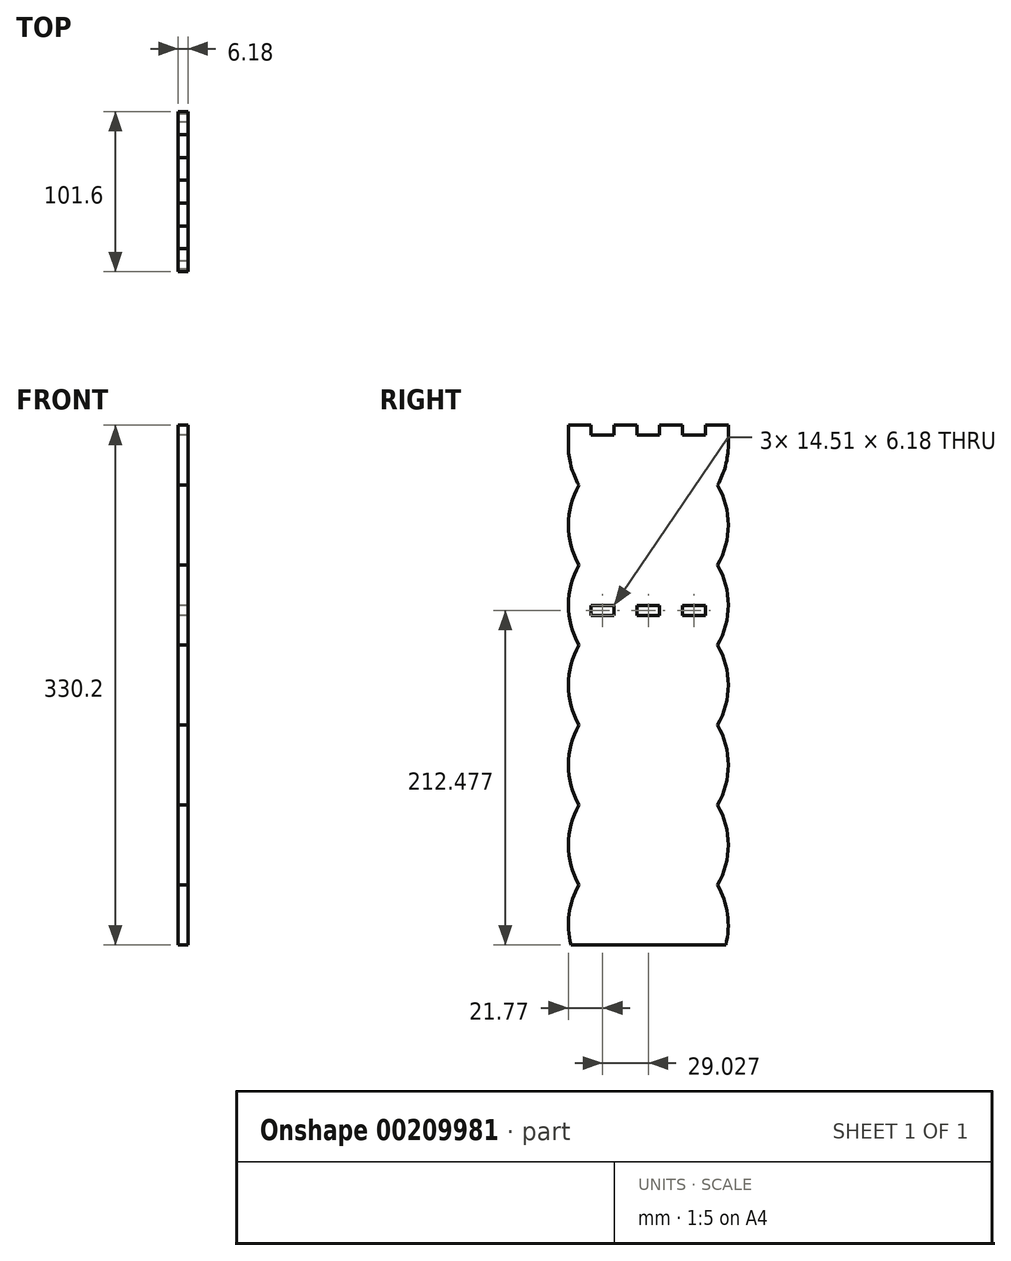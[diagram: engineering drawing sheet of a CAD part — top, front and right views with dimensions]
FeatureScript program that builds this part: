
annotation { "Feature Type Name" : "Feature", "Feature Type Description" : "" }
export const myFeature = defineFeature(function(context is Context, id is Id, definition is map)
    precondition{}
    {
        {
            var Q0;
            Q0=qCreatedBy(makeId("Right.planeOp"),FACE);
            var sketch = newSketch(context, id + "F0", { "sketchPlane" : qUnion([Q0])});
            skLineSegment(sketch, "E0.bottom", {"start": v(49.19, -165.1) * mm, "end": v(-49.19, -165.1) * mm});
            skLineSegment(sketch, "E0.top", {"start": v(50.8, 165.1) * mm, "end": v(36.28, 165.1) * mm});
            skPoint(sketch, "E0.middle", {"position": v(0, 0) * mm});
            skArc(sketch, "E1", {"start": v(-44, 25.4) * mm, "mid": v(-50.8, 0) * mm, "end": v(-44, -25.4) * mm});
            skArc(sketch, "E2", {"start": v(-44, 76.2) * mm, "mid": v(-50.8, 50.8) * mm, "end": v(-44, 25.4) * mm});
            skArc(sketch, "E3", {"start": v(-44, 127) * mm, "mid": v(-50.8, 101.6) * mm, "end": v(-44, 76.2) * mm});
            skArc(sketch, "E4", {"start": v(-50.8, 152.4) * mm, "mid": v(-49.07, 139.25) * mm, "end": v(-44, 127) * mm});
            skArc(sketch, "E5", {"start": v(-44, -25.4) * mm, "mid": v(-50.8, -50.8) * mm, "end": v(-44, -76.2) * mm});
            skArc(sketch, "E6", {"start": v(-44, -76.2) * mm, "mid": v(-50.8, -101.6) * mm, "end": v(-44, -127) * mm});
            skArc(sketch, "E7", {"start": v(-44, -127) * mm, "mid": v(-50.33, -145.54) * mm, "end": v(-49.19, -165.1) * mm});
            skPoint(sketch, "E8.orphan", {"position": v(0, 165.1) * mm});
            skLineSegment(sketch, "E9.trimOffspring", {"start": v(-50.8, 152.4) * mm, "end": v(-50.8, 165.1) * mm});
            skLineSegment(sketch, "E10.trimOffspring", {"start": v(50.8, 152.4) * mm, "end": v(50.8, 165.1) * mm});
            skArc(sketch, "E11.trimOffspring", {"start": v(44, 76.2) * mm, "mid": v(50.8, 101.6) * mm, "end": v(44, 127) * mm});
            skArc(sketch, "E12.trimOffspring", {"start": v(44, 127) * mm, "mid": v(49.07, 139.25) * mm, "end": v(50.8, 152.4) * mm});
            skArc(sketch, "E13.trimOffspring", {"start": v(44, 25.4) * mm, "mid": v(50.8, 50.8) * mm, "end": v(44, 76.2) * mm});
            skArc(sketch, "E14.trimOffspring", {"start": v(44, -25.4) * mm, "mid": v(50.8, 0) * mm, "end": v(44, 25.4) * mm});
            skArc(sketch, "E15.trimOffspring", {"start": v(44, -76.2) * mm, "mid": v(50.8, -50.8) * mm, "end": v(44, -25.4) * mm});
            skArc(sketch, "E16.trimOffspring", {"start": v(44, -127) * mm, "mid": v(50.8, -101.6) * mm, "end": v(44, -76.2) * mm});
            skArc(sketch, "E17.trimOffspring", {"start": v(49.19, -165.1) * mm, "mid": v(50.33, -145.54) * mm, "end": v(44, -127) * mm});
            skPoint(sketch, "E18.trimOffspring.end.orphan", {"position": v(0, -165.1) * mm});
            skPoint(sketch, "E19.orphan", {"position": v(-50.8, -165.1) * mm});
            skPoint(sketch, "E20.orphan", {"position": v(50.8, -165.1) * mm});
            skLineSegment(sketch, "E21", {"start": v(-36.29, 165.1) * mm, "end": v(-36.29, 158.92) * mm});
            skLineSegment(sketch, "E22", {"start": v(-36.29, 158.92) * mm, "end": v(-21.77, 158.92) * mm});
            skLineSegment(sketch, "E23", {"start": v(-21.77, 158.92) * mm, "end": v(-21.77, 165.1) * mm});
            skLineSegment(sketch, "E24", {"start": v(-7.26, 165.1) * mm, "end": v(-7.26, 158.92) * mm});
            skLineSegment(sketch, "E25", {"start": v(-7.26, 158.92) * mm, "end": v(0, 158.92) * mm});
            skLineSegment(sketch, "E26.trimOffspring", {"start": v(-36.29, 165.1) * mm, "end": v(-50.8, 165.1) * mm});
            skLineSegment(sketch, "E27.MirrorCS", {"start": v(7.25, 158.92) * mm, "end": v(0, 158.92) * mm});
            skLineSegment(sketch, "E28.MirrorCS", {"start": v(7.25, 165.1) * mm, "end": v(7.25, 158.92) * mm});
            skLineSegment(sketch, "E29.MirrorCS", {"start": v(36.28, 158.92) * mm, "end": v(21.77, 158.92) * mm});
            skLineSegment(sketch, "E30.MirrorCS", {"start": v(-50.8, 165.1) * mm, "end": v(-36.29, 165.1) * mm});
            skLineSegment(sketch, "E31.MirrorCS", {"start": v(36.28, 165.1) * mm, "end": v(36.28, 158.92) * mm});
            skLineSegment(sketch, "E32.MirrorCS", {"start": v(21.77, 158.92) * mm, "end": v(21.77, 165.1) * mm});
            skLineSegment(sketch, "E33.trimOffspring", {"start": v(0, 165.1) * mm, "end": v(0, 165.1) * mm});
            skLineSegment(sketch, "E34.trimOffspring", {"start": v(7.25, 165.1) * mm, "end": v(21.77, 165.1) * mm});
            skLineSegment(sketch, "E35.trimOffspring", {"start": v(-21.77, 165.1) * mm, "end": v(-7.26, 165.1) * mm});
            skLineSegment(sketch, "E36", {"start": v(0, 50.8) * mm, "end": v(0, 50.47) * mm});
            skLineSegment(sketch, "E37", {"start": v(50.7, 104.7) * mm, "end": v(50.8, 104.7) * mm});
            skLineSegment(sketch, "E38.MirrorCS", {"start": v(0, 44.28) * mm, "end": v(0, 44.28) * mm});
            skPoint(sketch, "E39.MirrorP", {"position": v(0, 44.28) * mm});
            skLineSegment(sketch, "E40.MirrorCS", {"start": v(-50.8, 44.28) * mm, "end": v(-50.8, 44.28) * mm});
            skLineSegment(sketch, "E41.MirrorCS", {"start": v(7.25, 44.28) * mm, "end": v(7.25, 50.47) * mm});
            skLineSegment(sketch, "E42.MirrorCS", {"start": v(-36.29, 44.28) * mm, "end": v(-36.29, 50.47) * mm});
            skLineSegment(sketch, "E43.MirrorCS", {"start": v(-7.26, 50.47) * mm, "end": v(0, 50.47) * mm});
            skLineSegment(sketch, "E44.MirrorCS", {"start": v(-36.29, 50.47) * mm, "end": v(-21.77, 50.47) * mm});
            skLineSegment(sketch, "E45.MirrorCS", {"start": v(-7.26, 44.28) * mm, "end": v(-7.26, 50.47) * mm});
            skLineSegment(sketch, "E46.MirrorCS", {"start": v(-21.77, 50.47) * mm, "end": v(-21.77, 44.28) * mm});
            skLineSegment(sketch, "E47.MirrorCS", {"start": v(7.25, 50.47) * mm, "end": v(0, 50.47) * mm});
            skLineSegment(sketch, "E48.MirrorCS", {"start": v(36.28, 44.28) * mm, "end": v(36.28, 50.47) * mm});
            skLineSegment(sketch, "E49.MirrorCS", {"start": v(50.8, 44.28) * mm, "end": v(50.8, 44.28) * mm});
            skLineSegment(sketch, "E50.MirrorCS", {"start": v(36.28, 50.47) * mm, "end": v(21.77, 50.47) * mm});
            skLineSegment(sketch, "E51.MirrorCS", {"start": v(21.77, 50.47) * mm, "end": v(21.77, 44.28) * mm});
            skLineSegment(sketch, "E52", {"start": v(-36.29, 44.28) * mm, "end": v(-21.77, 44.28) * mm});
            skLineSegment(sketch, "E53", {"start": v(-7.26, 44.28) * mm, "end": v(7.25, 44.28) * mm});
            skLineSegment(sketch, "E54", {"start": v(21.77, 44.28) * mm, "end": v(36.28, 44.28) * mm});
            skPoint(sketch, "E55.orphan", {"position": v(-50.8, 56.98) * mm});
            skPoint(sketch, "E56.MirrorCS.start.orphan", {"position": v(50.8, 56.98) * mm});
            skPoint(sketch, "E57.orphan", {"position": v(50.8, 44.28) * mm});
            skPoint(sketch, "E58.MirrorCS.end.orphan", {"position": v(0, 158.58) * mm});
            skSolve(sketch);
        }
        {
            var Q0;
            Q0 = qSketchRegion(id + "F0", true);
            extrude(context, id + "F1", {"entities" : qUnion([Q0]), "depth" : 6.18 * mm});
        }
    });
